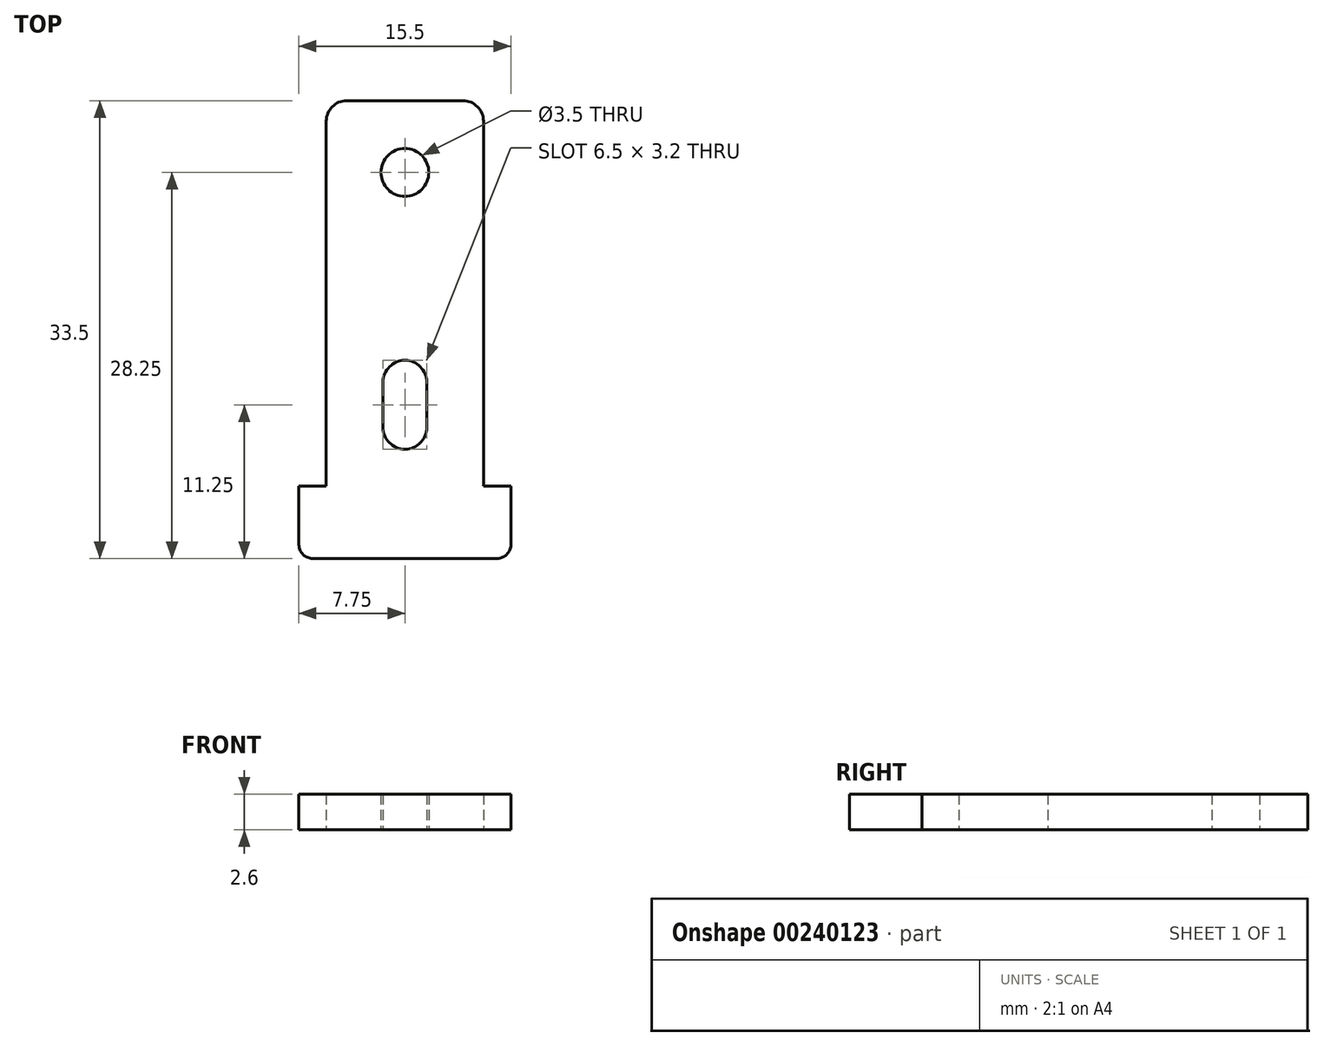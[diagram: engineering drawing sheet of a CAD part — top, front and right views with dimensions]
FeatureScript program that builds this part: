
annotation { "Feature Type Name" : "Feature", "Feature Type Description" : "" }
export const myFeature = defineFeature(function(context is Context, id is Id, definition is map)
    precondition{}
    {
        {
            var Q0;
            Q0=qCreatedBy(makeId("Top.planeOp"),FACE);
            var sketch = newSketch(context, id + "F0", { "sketchPlane" : qUnion([Q0])});
            skLineSegment(sketch, "E0", {"start": v(-13.5, 33.5) * mm, "end": v(-13.5, 5.3) * mm});
            skLineSegment(sketch, "E1", {"start": v(-13.5, 5.3) * mm, "end": v(-15.5, 5.3) * mm});
            skLineSegment(sketch, "E2", {"start": v(-15.5, 5.3) * mm, "end": v(-15.5, 0) * mm});
            skLineSegment(sketch, "E3", {"start": v(-15.5, 0) * mm, "end": v(0, 0) * mm});
            skLineSegment(sketch, "E4", {"start": v(0, 0) * mm, "end": v(0, 5.3) * mm});
            skLineSegment(sketch, "E5", {"start": v(0, 5.3) * mm, "end": v(-2, 5.3) * mm});
            skLineSegment(sketch, "E6", {"start": v(-2, 5.3) * mm, "end": v(-2, 33.5) * mm});
            skLineSegment(sketch, "E7", {"start": v(-2, 33.5) * mm, "end": v(-13.5, 33.5) * mm});
            skCircle(sketch, "E8", {"center": v(-7.75, 28.25) * mm, "radius": 1.75 * mm});
            skLineSegment(sketch, "E9", {"start": v(-7.75, 28.25) * mm, "end": v(-7.75, 33.5) * mm});
            skPoint(sketch, "E10", {"position": v(-7.75, 0) * mm});
            skCircle(sketch, "E11", {"center": v(-7.75, 9.6) * mm, "radius": 1.6 * mm});
            skCircle(sketch, "E12", {"center": v(-7.75, 12.9) * mm, "radius": 1.6 * mm});
            skLineSegment(sketch, "E13", {"start": v(-6.15, 9.6) * mm, "end": v(-6.15, 12.9) * mm});
            skLineSegment(sketch, "E14", {"start": v(-9.35, 9.6) * mm, "end": v(-9.35, 12.9) * mm});
            skSolve(sketch);
        }
        {
            var Q0;
            Q0 = qSketchRegion(id + "F0", true);
            extrude(context, id + "F1", {"entities" : qUnion([Q0]), "depth" : 2.6 * mm});
        }
        {
            var Q0;
            Q0=makeQuery(id+"F1.opExtrude","SWEPT_EDGE",EDGE,{"disambiguationData":[OSD([sQuery(id+"F0.wireOp",EDGE,"E0"),sQuery(id+"F0.wireOp",EDGE,"E7")])]});
            var Q1;
            Q1=makeQuery(id+"F1.opExtrude","SWEPT_EDGE",EDGE,{"disambiguationData":[OSD([sQuery(id+"F0.wireOp",EDGE,"E6"),sQuery(id+"F0.wireOp",EDGE,"E7")])]});
            fillet(context, id + "F2", {"entities" : qUnion([Q0, Q1]), "radius" : 1.5 * mm, "tangentPropagation" : true, "allowEdgeOverflow" : false});
        }
        {
            var Q0;
            Q0=makeQuery(id+"F1.opExtrude","SWEPT_EDGE",EDGE,{"disambiguationData":[OSD([sQuery(id+"F0.wireOp",EDGE,"E3"),sQuery(id+"F0.wireOp",EDGE,"E4")])]});
            var Q1;
            Q1=makeQuery(id+"F1.opExtrude","SWEPT_EDGE",EDGE,{"disambiguationData":[OSD([sQuery(id+"F0.wireOp",EDGE,"E2"),sQuery(id+"F0.wireOp",EDGE,"E3")])]});
            fillet(context, id + "F3", {"entities" : qUnion([Q0, Q1]), "radius" : 1 * mm, "tangentPropagation" : true, "allowEdgeOverflow" : false});
        }
    });
